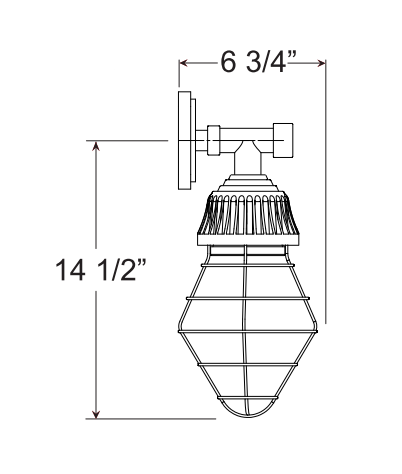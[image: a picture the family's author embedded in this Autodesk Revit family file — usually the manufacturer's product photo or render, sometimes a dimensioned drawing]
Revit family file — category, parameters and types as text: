
# Revit family: VBUTGUP110
name_source: partatom
category: Lighting Fixtures
units: mm (PartAtom-declared; Revit-internal decimal feet)

## family parameters
Always vertical = Yes
Cut with Voids When Loaded = No
Light Source = Yes
OmniClass Number = 23.80.70.00
OmniClass Title = Lighting
Part Type = Normal
Room Calculation Point = No
Round Connector Dimension = Use Diameter
Shared = No
Work Plane-Based = No

## types (3) — shared parameters
Apparent Load = 200 VA
Body Colour = Cast aluminium
Body Material = body
Bulb = Bulb
Color Filter = 16777215
Construction Material = Cast aluminum.
Default Elevation = 0' - 0"
Description = 120-277 Voltage
Dimming Lamp Color Temperature Shift = <None>
Fixture Height = 1' - 5"
INSIDE BODY = INSIDE BODY
Lamp = 200w Max Incandescent
Load Classification = Lighting
Manufacturer = ANP Lighting
Photometric Web File = generic.ies
Power Factor = 1
Tilt Angle = 90.00°
URL = https://www.anplighting.com
Voltage = 120 V
Warranty = 5 year limited warranty
Wattage Comments = 200W Max

## per-type parameters (varying)
| type | Fixture Diameter | Weight |
| VBUTGUP110-1 | 0' - 8" | 4.2 lbs |
| VBUTGUP110-2 | 1' - 4" | 5.9 lbs |
| VBUTGUP110-3 | 2' - 1" | 14.5 lbs |

note: column(s) folded — value = type name in every type: Model

type visibility flags: 3 boolean params named "<type name>" — each type sets only its own to Yes (folded from table)

## geometry (parser evidence)
native form markers: Sweep x8
no freeform markers — native parametric forms only
